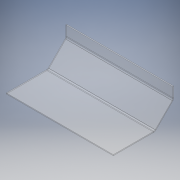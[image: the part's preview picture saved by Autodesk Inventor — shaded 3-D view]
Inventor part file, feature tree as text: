
AUTODESK INVENTOR PART (.ipt)
format: ipt  version: 2018 (Build 220112000, 112)  size: 163,840 bytes
history: native  units: mm
features: sheet_metal_op x7, sketch x3, other x3
ambient origin geometry x8: Origin, YZ Plane, XZ Plane, XY Plane, X Axis, Y Axis, Z Axis, Center Point
bodies: Solid1 (feature_tree)
feature tree (13):
  sheet_metal_op  "Face1"
  sheet_metal_op  "Flange1"
  sheet_metal_op  "Flange2"
  sketch  "Sketch1"  dims[d0=1100.0mm]
  other  "Plate1"
  sketch  "Sketch2"  dims[d1=430.0mm]
  other  "Plate2"
  sheet_metal_op  "Bend1"
  sheet_metal_op  "Corner1"
  sketch  "Sketch3"  dims[d2=10.0mm d3=10.0mm d4=5.0mm d5=20.0mm d6=10.0mm d7=270.0mm d8=45.0deg d9=20.0mm d10=40.0mm d11=10.0mm d12=10.0mm d13=10.0mm d14=5.0mm d15=20.0mm d16=10.0mm d17=120.0mm d18=45.0deg d19=20.0mm d20=40.0mm d21=10.0mm d22=10.0mm]
  other  "Plate3"
  sheet_metal_op  "Bend2"
  sheet_metal_op  "Corner2"
